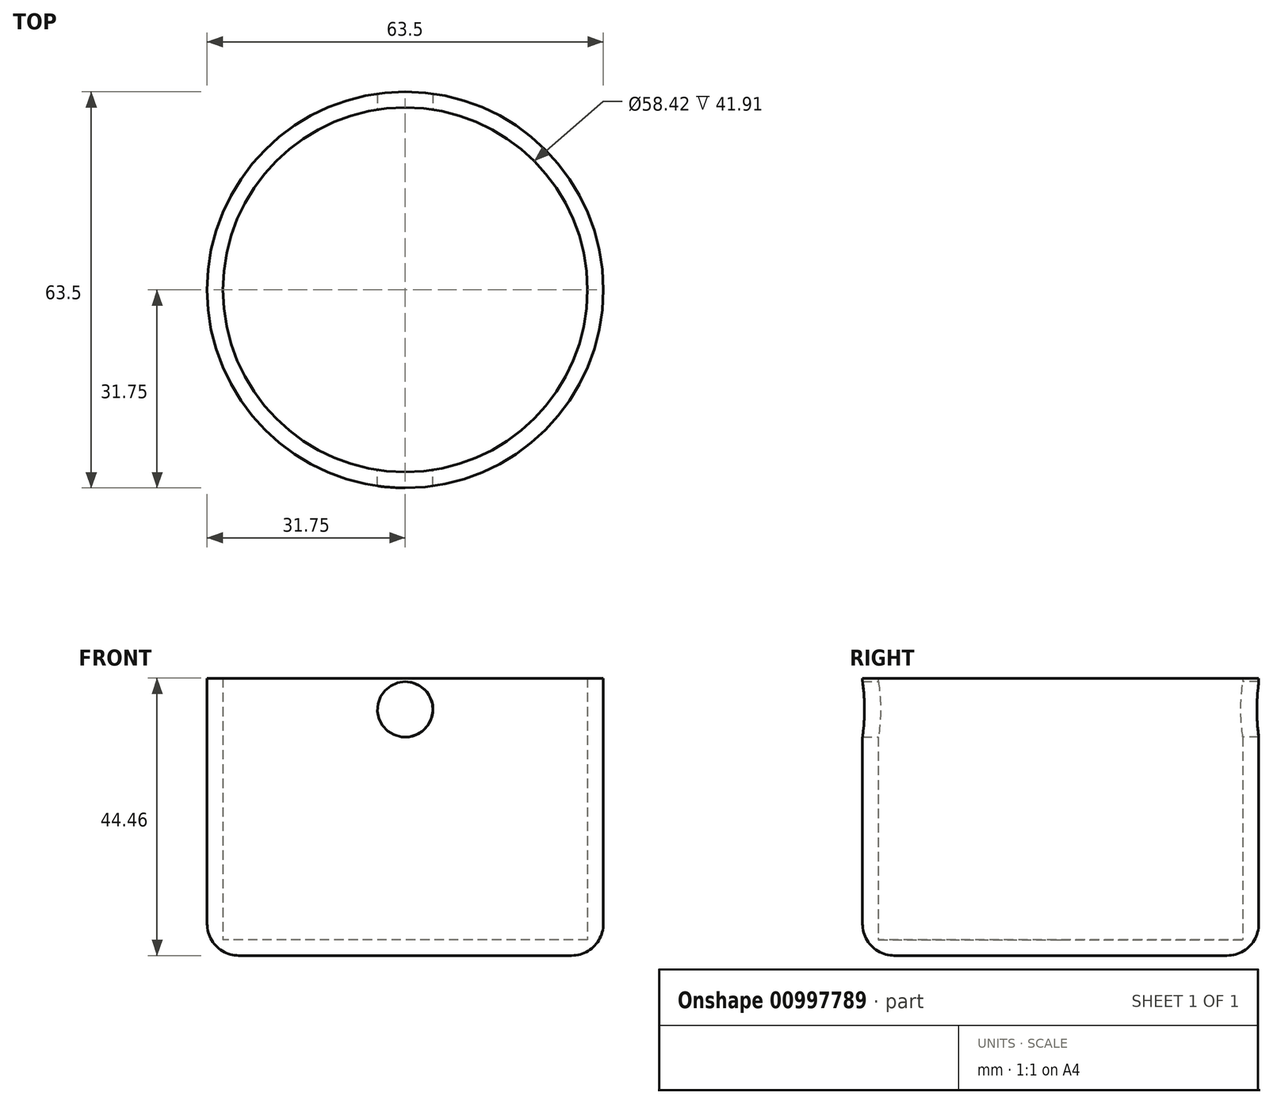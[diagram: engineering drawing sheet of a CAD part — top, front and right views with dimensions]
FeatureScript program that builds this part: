
annotation { "Feature Type Name" : "Feature", "Feature Type Description" : "" }
export const myFeature = defineFeature(function(context is Context, id is Id, definition is map)
    precondition{}
    {
        {
            var Q0;
            Q0=qCreatedBy(makeId("Top.planeOp"),FACE);
            var sketch = newSketch(context, id + "F0", { "sketchPlane" : qUnion([Q0])});
            skCircle(sketch, "E0", {"center": v(0, 0) * mm, "radius": 31.75 * mm});
            skSolve(sketch);
        }
        {
            var Q0;
            Q0 = qSketchRegion(id + "F0", true);
            extrude(context, id + "F1", {"entities" : qUnion([Q0]), "endBound" : BoundingType.SYMMETRIC, "depth" : 44.45 * mm, "offsetDistance" : 25.4 * mm});
        }
        {
            var Q0;
            Q0=makeQuery(id+"F1.opExtrude","CAP_FACE",FACE,{"disambiguationData":[OSD([sQuery(id+"F0.wireOp",EDGE,"E0")])],"isStart":false});
            shell(context, id + "F2", {"entities" : qUnion([Q0]), "thickness" : 2.54 * mm});
        }
        {
            var Q0;
            Q0=qCreatedBy(makeId("Front.planeOp"),FACE);
            var sketch = newSketch(context, id + "F3", { "sketchPlane" : qUnion([Q0])});
            skCircle(sketch, "E1", {"center": v(0, 17.22) * mm, "radius": 3.81 * mm});
            skSolve(sketch);
        }
        {
            var Q0;
            Q0=sQuery(id+"F3.wireOp",VERTEX,"E1.center");
            var Q1;
            Q1=makeQuery(id+"F1.opExtrude","SWEPT_BODY",BODY,{"disambiguationData":[OSD([sQuery(id+"F0.wireOp",EDGE,"E0")])]});
            hole(context, id + "F4", {"style" : HoleStyle.SIMPLE, "endStyle" : HoleEndStyle.THROUGH, "oppositeDirection" : true, "holeDiameter" : 8.9 * mm, "majorDiameter" : 6.35 * mm, "isTappedThrough" : true, "tappedDepth" : 12.7 * mm, "tapClearance" : 3, "locations" : qUnion([Q0]), "scope" : qUnion([Q1])});
        }
        {
            var Q0;
            Q0=sQuery(id+"F3.wireOp",VERTEX,"E1.center");
            var Q1;
            Q1=makeQuery(id+"F1.opExtrude","SWEPT_BODY",BODY,{"disambiguationData":[OSD([sQuery(id+"F0.wireOp",EDGE,"E0")])]});
            hole(context, id + "F5", {"style" : HoleStyle.SIMPLE, "endStyle" : HoleEndStyle.THROUGH, "holeDiameter" : 8.9 * mm, "majorDiameter" : 6.35 * mm, "isTappedThrough" : true, "tappedDepth" : 12.7 * mm, "tapClearance" : 3, "locations" : qUnion([Q0]), "scope" : qUnion([Q1])});
        }
        {
            var Q0;
            Q0=makeQuery(id+"F1.opExtrude","CAP_EDGE",EDGE,{"disambiguationData":[OSD([sQuery(id+"F0.wireOp",EDGE,"E0")])],"isStart":true});
            fillet(context, id + "F6", {"entities" : qUnion([Q0]), "radius" : 5.08 * mm, "tangentPropagation" : true, "allowEdgeOverflow" : false});
        }
    });
